# Revit family: Lighting-Industrial-GEWISS-ESALITE-HB-HIGHBAYS-LED_16K_DALI
name_source: partatom
category: Apparecchi per illuminazione
units: mm (PartAtom-declared; Revit-internal decimal feet)

## family parameters
Condiviso = No
Host = Superficie
Punto di calcolo locali = Sì
Quota connettore circolare = Usa diametro
Sorgente d'illuminazione = No
Taglio con vuoti quando caricato = No
Tipo di parte = Normale

## types (1)
- Lighting-Industrial-GEWISS-ESALITE-HB-HIGHBAYS-LED_16K_DALI
    Application = Indoor / Outdoor
    Catalogue = LIGHTING
    Catalogue Range = ESALITE HB - 16K
    Colour = Grey RAL 9006
    Colour temperature: = 5700 K (CRI>80)
    Descrizione = ESALITE 16K ELL.5700K PLAF+V.GR.DALI
    Driver type = Driver Led Dali
    Efficiency class of integrated LEDs = A ÷ A++
    Electrocod = 2444
    IDF = 52d9f25e-ae7e-4c7c-a9a9-41bfd309ca57
    IDT = a54f4c13e4cb438fafd2955485c5441c
    IP degree = IP66
    Immagine tipo = ESALITE_HB.jpg
    Insulation class = I
    LED current. = 0,599999999999999A
    Lamp- = LED - Not replaceable
    Life time L90B10 (Tq 25°C) = 100000H
    Life time L90B10 (Tq 50°C) = 50000H
    Lumen output (lm) = 13600
    Modello = GWS6335GD57K
    Nominal flux (lm) = 17000
    Operating temperature: = -30 +50 °C
    Optic = Elliptical
    Overvoltage resistance : = Common mode: 8KV; Differential mode: 6KV
    Potenza di sitema = Wxxx
    Produttore = GEWISS S.p.A.
    Prospetto di default = 1219 mm
    SEO = High bay
    Shield type = Tempered glass
    Shock resistance = IK08
    System power = 125W
    Technical sheet = https://www.gewiss.com
    URL = https://www.gewiss.com
    Version file RFA = 20.11
    Versions = 5700K cold light
    Voltage- = 220/240 V - 50/60 Hz
    Warranty = 5 years
    Weight (kg): = 7,5
